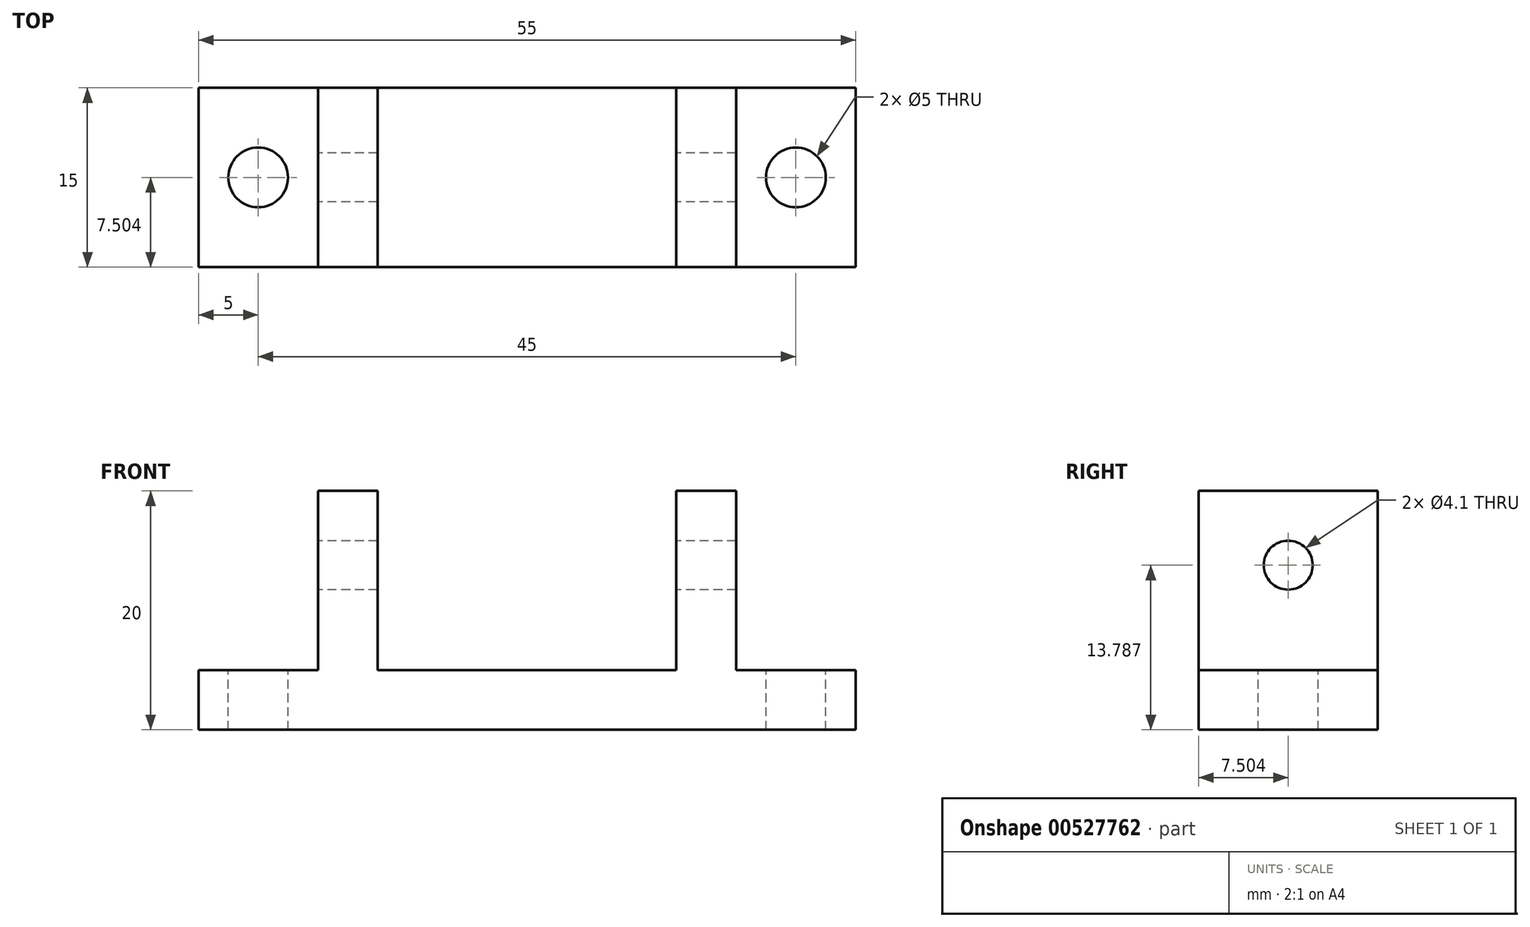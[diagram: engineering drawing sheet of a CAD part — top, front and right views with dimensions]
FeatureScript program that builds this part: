
annotation { "Feature Type Name" : "Feature", "Feature Type Description" : "" }
export const myFeature = defineFeature(function(context is Context, id is Id, definition is map)
    precondition{}
    {
        {
            var Q0;
            Q0=qCreatedBy(makeId("Top.planeOp"),FACE);
            var sketch = newSketch(context, id + "F0", { "sketchPlane" : qUnion([Q0])});
            skLineSegment(sketch, "E0.bottom", {"start": v(-15.34, 8.5) * mm, "end": v(39.66, 8.5) * mm});
            skLineSegment(sketch, "E0.top", {"start": v(-15.34, -6.5) * mm, "end": v(39.66, -6.5) * mm});
            skLineSegment(sketch, "E0.left", {"start": v(-15.34, 8.5) * mm, "end": v(-15.34, -6.5) * mm});
            skLineSegment(sketch, "E0.right", {"start": v(39.66, 8.5) * mm, "end": v(39.66, -6.5) * mm});
            skSolve(sketch);
        }
        {
            var Q0;
            Q0 = qSketchRegion(id + "F0", true);
            extrude(context, id + "F1", {"entities" : qUnion([Q0]), "depth" : 5 * mm, "offsetDistance" : 25 * mm});
        }
        {
            var Q0;
            Q0=makeQuery(id+"F1.opExtrude","CAP_FACE",FACE,{"disambiguationData":[OSD([sQuery(id+"F0.wireOp",EDGE,"E0.bottom"),sQuery(id+"F0.wireOp",EDGE,"E0.top"),sQuery(id+"F0.wireOp",EDGE,"E0.left"),sQuery(id+"F0.wireOp",EDGE,"E0.right")])],"isStart":false});
            var sketch = newSketch(context, id + "F2", { "sketchPlane" : qUnion([Q0])});
            skLineSegment(sketch, "E1.bottom", {"start": v(-5.34, 8.5) * mm, "end": v(-0.34, 8.5) * mm});
            skLineSegment(sketch, "E1.top", {"start": v(-5.34, -6.5) * mm, "end": v(-0.34, -6.5) * mm});
            skLineSegment(sketch, "E1.left", {"start": v(-5.34, 8.5) * mm, "end": v(-5.34, -6.5) * mm});
            skLineSegment(sketch, "E1.right", {"start": v(-0.34, 8.5) * mm, "end": v(-0.34, -6.5) * mm});
            skLineSegment(sketch, "E2.bottom", {"start": v(24.66, 8.5) * mm, "end": v(29.66, 8.5) * mm});
            skLineSegment(sketch, "E2.top", {"start": v(24.66, -6.5) * mm, "end": v(29.66, -6.5) * mm});
            skLineSegment(sketch, "E2.left", {"start": v(24.66, 8.5) * mm, "end": v(24.66, -6.5) * mm});
            skLineSegment(sketch, "E2.right", {"start": v(29.66, 8.5) * mm, "end": v(29.66, -6.5) * mm});
            skSolve(sketch);
        }
        {
            var Q0;
            Q0 = qSketchRegion(id + "F2", true);
            extrude(context, id + "F3", {"entities" : qUnion([Q0]), "operationType" : NewBodyOperationType.ADD, "depth" : 15 * mm, "offsetDistance" : 25 * mm});
        }
        {
            var Q0;
            {var subQ0=sQuery(id+"F0.wireOp",EDGE,"E0.left");var subQ1=sQuery(id+"F0.wireOp",EDGE,"E0.top");var subQ2=sQuery(id+"F0.wireOp",EDGE,"E0.bottom");Q0=makeQuery(id+"F3.boolean.opBoolean","SPLIT",FACE,{"disambiguationData":[TD([makeQuery(id+"F1.opExtrude","SWEPT_FACE",FACE,{"disambiguationData":[OSD([subQ0])]})])],"derivedFrom":makeQuery(id+"F1.opExtrude","CAP_FACE",FACE,{"disambiguationData":[OSD([subQ2,subQ1,subQ0,sQuery(id+"F0.wireOp",EDGE,"E0.right")])],"isStart":false})});}
            var sketch = newSketch(context, id + "F4", { "sketchPlane" : qUnion([Q0])});
            skCircle(sketch, "E3", {"center": v(-10.34, 1) * mm, "radius": 2.5 * mm});
            skSolve(sketch);
        }
        {
            var Q0;
            Q0 = qSketchRegion(id + "F4", true);
            extrude(context, id + "F5", {"entities" : qUnion([Q0]), "operationType" : NewBodyOperationType.REMOVE, "oppositeDirection" : true, "depth" : 25 * mm, "offsetDistance" : 25 * mm});
        }
        {
            var Q0;
            {var subQ0=sQuery(id+"F0.wireOp",EDGE,"E0.top");var subQ1=sQuery(id+"F0.wireOp",EDGE,"E0.right");var subQ2=sQuery(id+"F0.wireOp",EDGE,"E0.bottom");Q0=makeQuery(id+"F3.boolean.opBoolean","SPLIT",FACE,{"disambiguationData":[TD([makeQuery(id+"F1.opExtrude","SWEPT_FACE",FACE,{"disambiguationData":[OSD([subQ1])]})])],"derivedFrom":makeQuery(id+"F1.opExtrude","CAP_FACE",FACE,{"disambiguationData":[OSD([subQ2,subQ0,sQuery(id+"F0.wireOp",EDGE,"E0.left"),subQ1])],"isStart":false})});}
            var sketch = newSketch(context, id + "F6", { "sketchPlane" : qUnion([Q0])});
            skCircle(sketch, "E4", {"center": v(34.66, 1) * mm, "radius": 2.5 * mm});
            skSolve(sketch);
        }
        {
            var Q0;
            Q0 = qSketchRegion(id + "F6", true);
            extrude(context, id + "F7", {"entities" : qUnion([Q0]), "operationType" : NewBodyOperationType.REMOVE, "oppositeDirection" : true, "depth" : 25 * mm, "offsetDistance" : 25 * mm});
        }
        {
            var Q0;
            Q0=makeQuery(id+"F3.opExtrude","SWEPT_FACE",FACE,{"disambiguationData":[OSD([sQuery(id+"F2.wireOp",EDGE,"E1.left")])]});
            var sketch = newSketch(context, id + "F8", { "sketchPlane" : qUnion([Q0])});
            skCircle(sketch, "E5", {"center": v(-1, 13.79) * mm, "radius": 2.05 * mm});
            skSolve(sketch);
        }
        {
            var Q0;
            Q0 = qSketchRegion(id + "F8", true);
            extrude(context, id + "F9", {"entities" : qUnion([Q0]), "operationType" : NewBodyOperationType.REMOVE, "endBound" : BoundingType.THROUGH_ALL, "oppositeDirection" : true, "depth" : 25 * mm, "offsetDistance" : 25 * mm});
        }
    });
